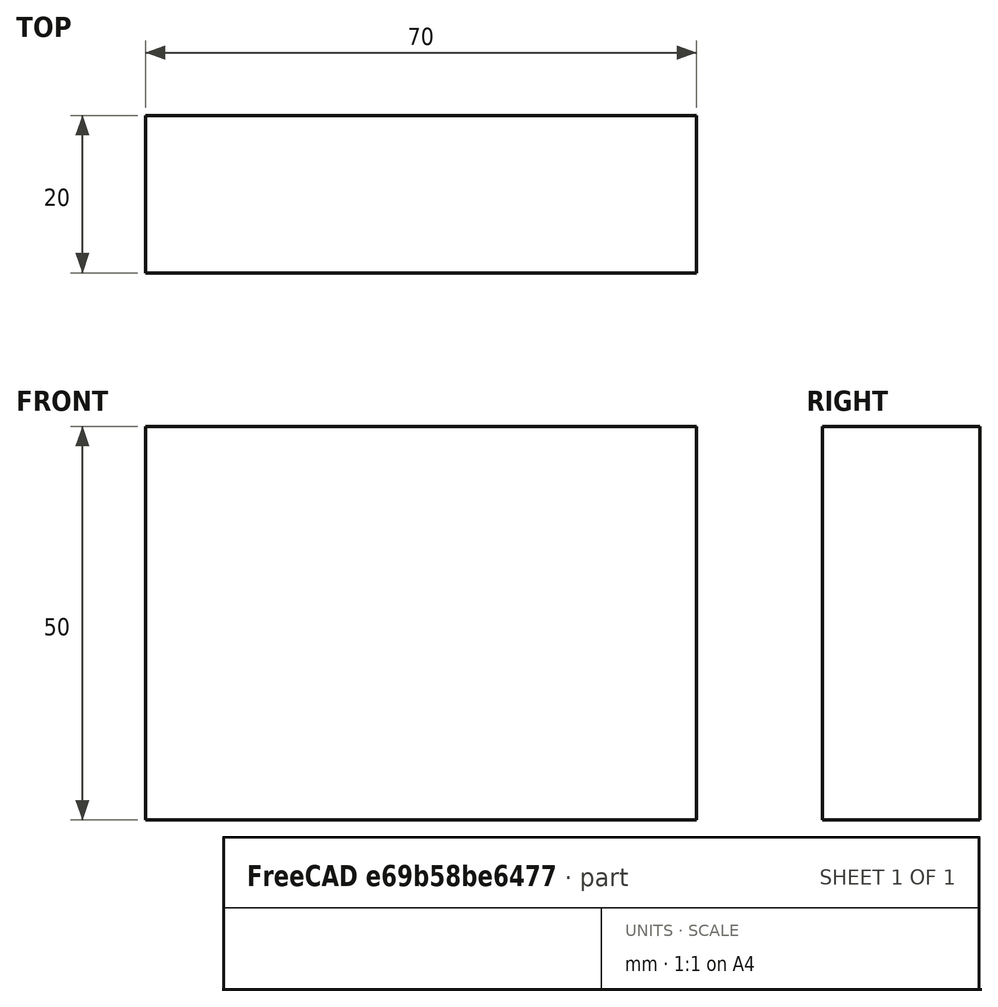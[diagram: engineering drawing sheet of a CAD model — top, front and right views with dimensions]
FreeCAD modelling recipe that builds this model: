
FCSTD DOCUMENT  (FreeCAD 0.15R4671 (Git))
Label: Flat Bar 70x20 EN10058 S235JR
License: All rights reserved
LicenseURL: http://en.wikipedia.org/wiki/All_rights_reserved
objects: Sketcher::SketchObject×1, Part::Extrusion×1
note: 2 computed .brp shape members not serialized (recipe doc carries the construction recipe); baked Part::Feature solids carry a one-line shape summary decoded from their .brp

FEATURE [Sketcher::SketchObject] Sketch
  sketch-geometry (4):
    g0: LineSegment StartX=-35 StartY=-10 StartZ=0 EndX=35 EndY=-10 EndZ=0
    g1: LineSegment StartX=35 StartY=-10 StartZ=0 EndX=35 EndY=10 EndZ=0
    g2: LineSegment StartX=35 StartY=10 StartZ=0 EndX=-35 EndY=10 EndZ=0
    g3: LineSegment StartX=-35 StartY=10 StartZ=0 EndX=-35 EndY=-10 EndZ=0
  constraints (12):
    c: Coincident(g0,g1)
    c: Coincident(g1,g2)
    c: Coincident(g2,g3)
    c: Coincident(g3,g0)
    c: Horizontal(g0)
    c: Horizontal(g2)
    c: Vertical(g1)
    c: Vertical(g3)
    c: Symmetric(g1,g2,g-2)
    c: Symmetric(g0,g1,g-1)
    c: DistanceY(g1) = 20
    c: DistanceX(g0) = 70
FEATURE [Part::Extrusion] Extrude  label="Flat Bar 70x20 EN10058 S235JR"
  Base = -> Sketch
  Dir = (0,0,50)
  Solid = true
